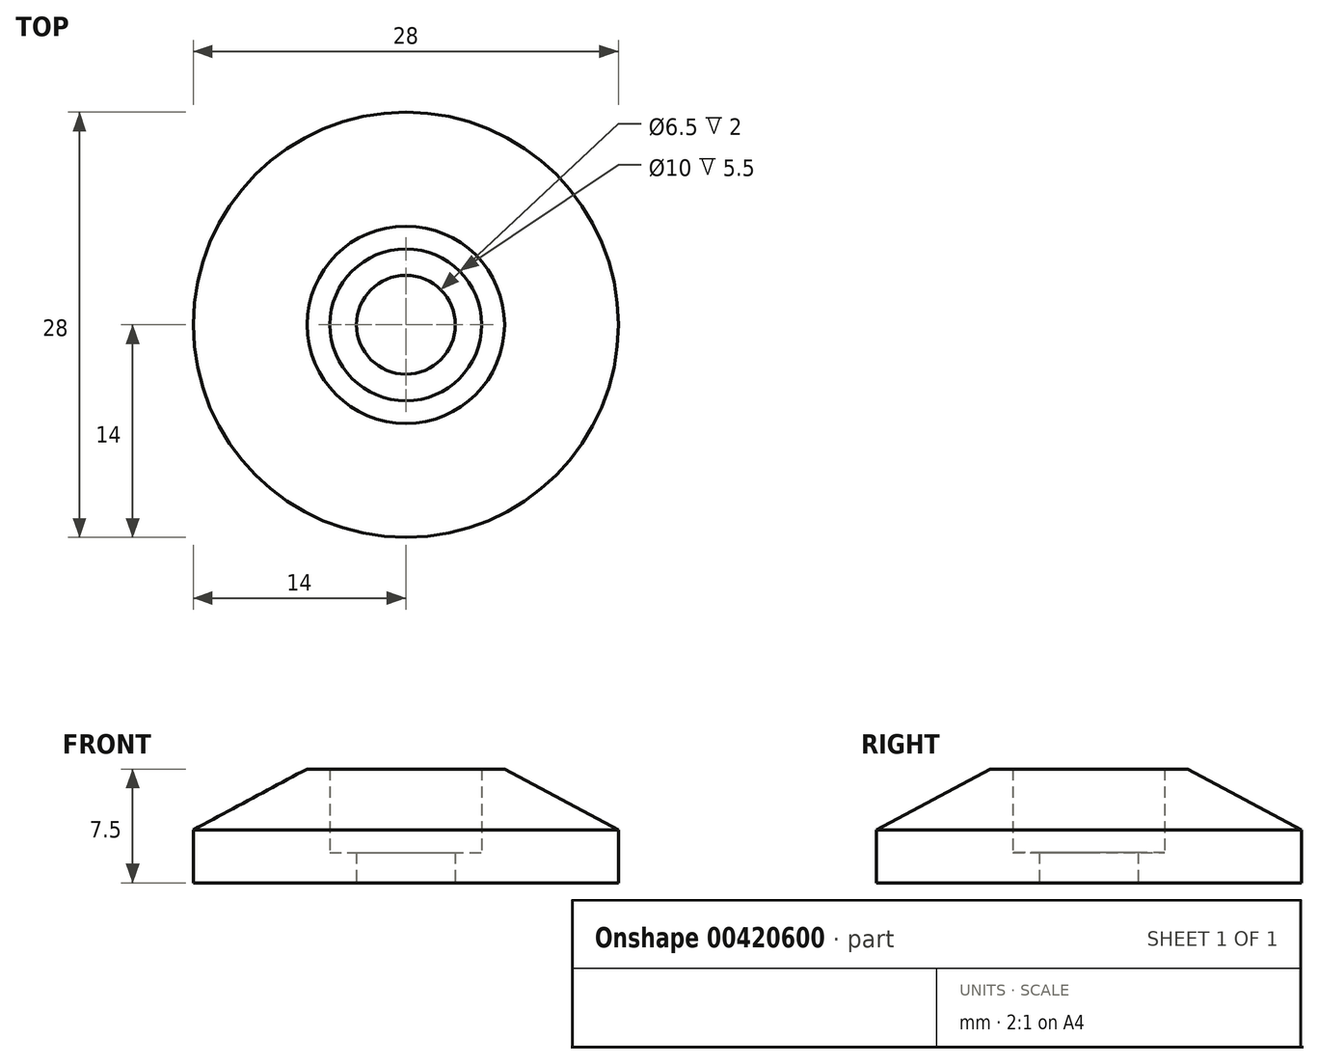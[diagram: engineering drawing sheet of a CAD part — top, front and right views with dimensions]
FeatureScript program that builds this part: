
annotation { "Feature Type Name" : "Feature", "Feature Type Description" : "" }
export const myFeature = defineFeature(function(context is Context, id is Id, definition is map)
    precondition{}
    {
        {
            var Q0;
            Q0=qCreatedBy(makeId("Front.planeOp"),FACE);
            var sketch = newSketch(context, id + "F0", { "sketchPlane" : qUnion([Q0])});
            skLineSegment(sketch, "E0", {"start": v(0, 0) * mm, "end": v(0, 13.35) * mm, "construction": true});
            skLineSegment(sketch, "E1", {"start": v(-3.25, 0) * mm, "end": v(-3.25, 2) * mm});
            skLineSegment(sketch, "E2", {"start": v(-3.25, 2) * mm, "end": v(-5, 2) * mm});
            skLineSegment(sketch, "E3", {"start": v(-5, 2) * mm, "end": v(-5, 7.5) * mm});
            skLineSegment(sketch, "E4", {"start": v(-5, 7.5) * mm, "end": v(-6.5, 7.5) * mm});
            skLineSegment(sketch, "E5", {"start": v(-6.5, 7.5) * mm, "end": v(-14, 3.5) * mm});
            skLineSegment(sketch, "E6", {"start": v(-14, 3.5) * mm, "end": v(-14, 0) * mm});
            skLineSegment(sketch, "E7", {"start": v(-14, 0) * mm, "end": v(-3.25, 0) * mm});
            skLineSegment(sketch, "E8", {"start": v(-3.25, 0) * mm, "end": v(0, 0) * mm, "construction": true});
            skSolve(sketch);
        }
        {
            var Q0;
            Q0 = qSketchRegion(id + "F0", true);
            var Q1;
            Q1=sQuery(id+"F0.wireOp",EDGE,"E0");
            revolve(context, id + "F1", {"entities" : qUnion([Q0]), "axis" : qUnion([Q1]), "revolveType" : RevolveType.FULL});
        }
    });
